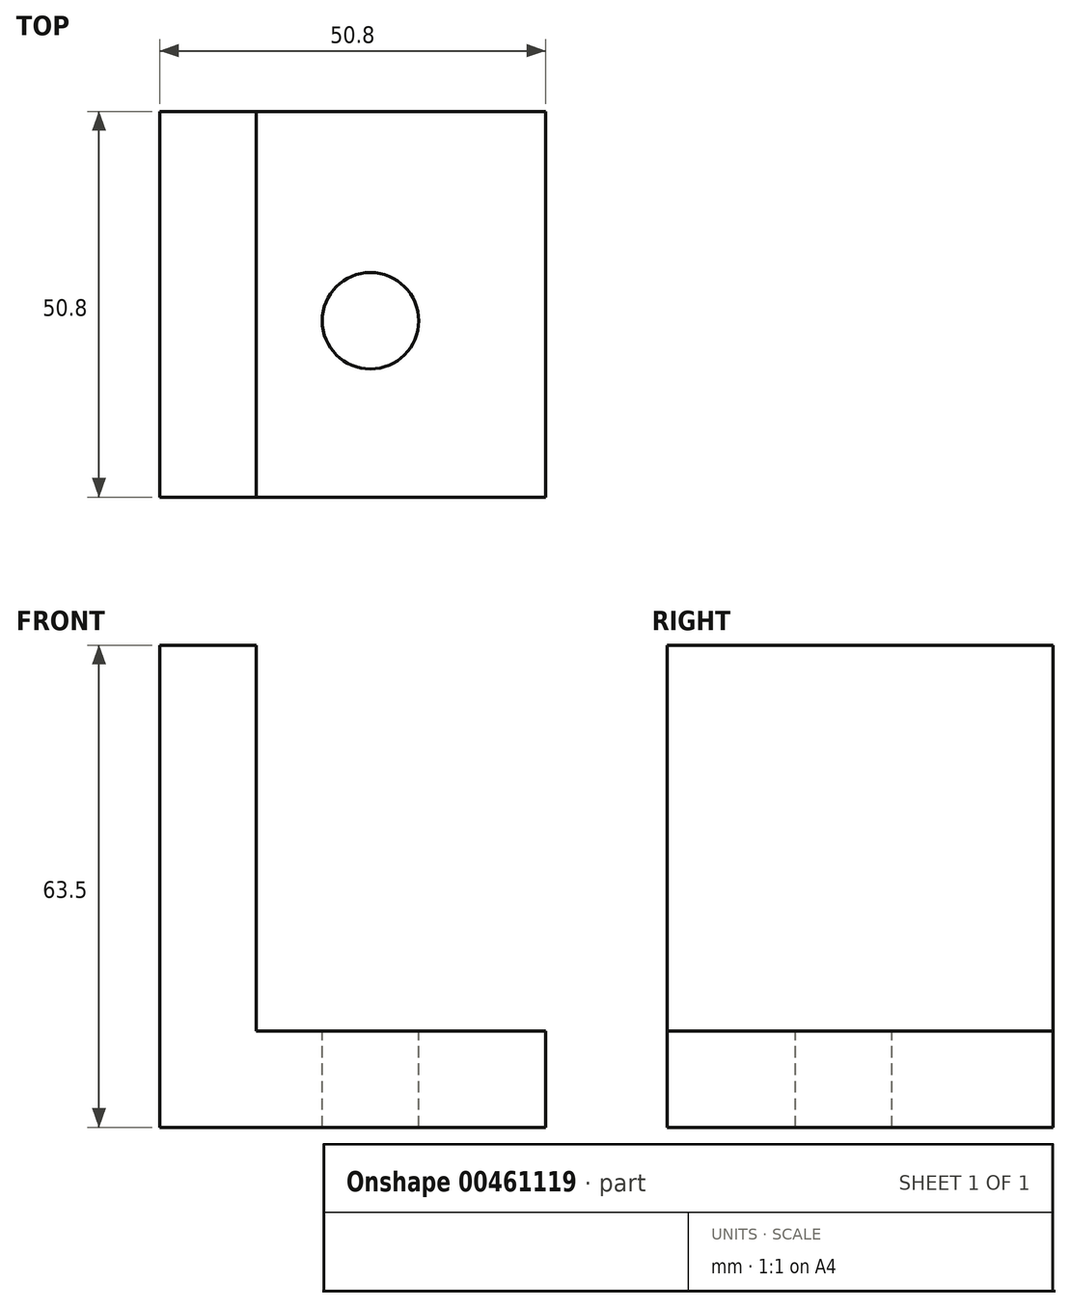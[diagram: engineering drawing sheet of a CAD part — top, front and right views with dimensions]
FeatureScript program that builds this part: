
annotation { "Feature Type Name" : "Feature", "Feature Type Description" : "" }
export const myFeature = defineFeature(function(context is Context, id is Id, definition is map)
    precondition{}
    {
        {
            var Q0;
            Q0=qCreatedBy(makeId("Top.planeOp"),FACE);
            var sketch = newSketch(context, id + "F0", { "sketchPlane" : qUnion([Q0])});
            skLineSegment(sketch, "E0.bottom", {"start": v(-22.8, 27.58) * mm, "end": v(28, 27.58) * mm});
            skLineSegment(sketch, "E0.top", {"start": v(-22.8, -23.22) * mm, "end": v(28, -23.22) * mm});
            skLineSegment(sketch, "E0.left", {"start": v(-22.8, 27.58) * mm, "end": v(-22.8, -23.22) * mm});
            skLineSegment(sketch, "E0.right", {"start": v(28, 27.58) * mm, "end": v(28, -23.22) * mm});
            skLineSegment(sketch, "E1", {"start": v(-22.8, 27.58) * mm, "end": v(-10.1, 27.58) * mm});
            skLineSegment(sketch, "E2", {"start": v(-10.1, 27.58) * mm, "end": v(-10.1, -23.22) * mm});
            skSolve(sketch);
        }
        {
            var Q0;
            Q0=makeQuery(id+"F0.imprint","IMPRINT",FACE,{"disambiguationData":[TD([[makeQuery(id+"F0.imprint","IMPRINT",EDGE,{"derivedFrom":sQuery(id+"F0.wireOp",EDGE,"E0.bottom")}),-1.0]])]});
            var Q1;
            {var subQ0=sQuery(id+"F0.wireOp",EDGE,"E0.left");Q1=makeQuery(id+"F0.imprint","IMPRINT",FACE,{"disambiguationData":[TD([[makeQuery(id+"F0.imprint","IMPRINT",EDGE,{"derivedFrom":subQ0}),1.0]])]});}
            extrude(context, id + "F1", {"entities" : qUnion([Q0, Q1]), "depth" : 12.7 * mm});
        }
        {
            var Q0;
            Q0=makeQuery(id+"F1.opExtrude","CAP_FACE",FACE,{"disambiguationData":[OSD([sQuery(id+"F0.wireOp",EDGE,"E0.bottom"),sQuery(id+"F0.wireOp",EDGE,"E0.top"),sQuery(id+"F0.wireOp",EDGE,"E0.left"),sQuery(id+"F0.wireOp",EDGE,"E0.right"),sQuery(id+"F0.wireOp",EDGE,"E1")])],"isStart":false});
            var sketch = newSketch(context, id + "F2", { "sketchPlane" : qUnion([Q0])});
            skLineSegment(sketch, "E3", {"start": v(-22.8, 27.58) * mm, "end": v(-10.1, 27.58) * mm});
            skLineSegment(sketch, "E4", {"start": v(-10.1, 27.58) * mm, "end": v(-10.1, -23.22) * mm});
            skSolve(sketch);
        }
        {
            var Q0;
            Q0=makeQuery(id+"F2.imprint","IMPRINT",FACE,{"disambiguationData":[TD([[makeQuery(id+"F2.imprint","IMPRINT",EDGE,{"derivedFrom":sQuery(id+"F2.wireOp",EDGE,"E3")}),-1.0]])]});
            extrude(context, id + "F3", {"entities" : qUnion([Q0]), "operationType" : NewBodyOperationType.ADD, "depth" : 50.8 * mm});
        }
        {
            var Q0;
            Q0=makeQuery(id+"F1.opExtrude","CAP_FACE",FACE,{"disambiguationData":[OSD([sQuery(id+"F0.wireOp",EDGE,"E0.bottom"),sQuery(id+"F0.wireOp",EDGE,"E0.top"),sQuery(id+"F0.wireOp",EDGE,"E0.left"),sQuery(id+"F0.wireOp",EDGE,"E0.right"),sQuery(id+"F0.wireOp",EDGE,"E1")])],"isStart":false});
            var sketch = newSketch(context, id + "F4", { "sketchPlane" : qUnion([Q0])});
            skCircle(sketch, "E5", {"center": v(4.93, 0) * mm, "radius": 6.35 * mm});
            skSolve(sketch);
        }
        {
            var Q0;
            Q0=sQuery(id+"F4.wireOp",VERTEX,"E5.center");
            var Q1;
            Q1=makeQuery(id+"F1.opExtrude","SWEPT_BODY",BODY,{"disambiguationData":[OSD([sQuery(id+"F0.wireOp",EDGE,"E0.bottom"),sQuery(id+"F0.wireOp",EDGE,"E0.top"),sQuery(id+"F0.wireOp",EDGE,"E0.left"),sQuery(id+"F0.wireOp",EDGE,"E0.right"),sQuery(id+"F0.wireOp",EDGE,"E1")])]});
            hole(context, id + "F5", {"style" : HoleStyle.SIMPLE, "endStyle" : HoleEndStyle.THROUGH, "holeDiameter" : 12.7 * mm, "isTappedThrough" : true, "tappedDepth" : 12.7 * mm, "tapClearance" : 3, "locations" : qUnion([Q0]), "scope" : qUnion([Q1])});
        }
    });
